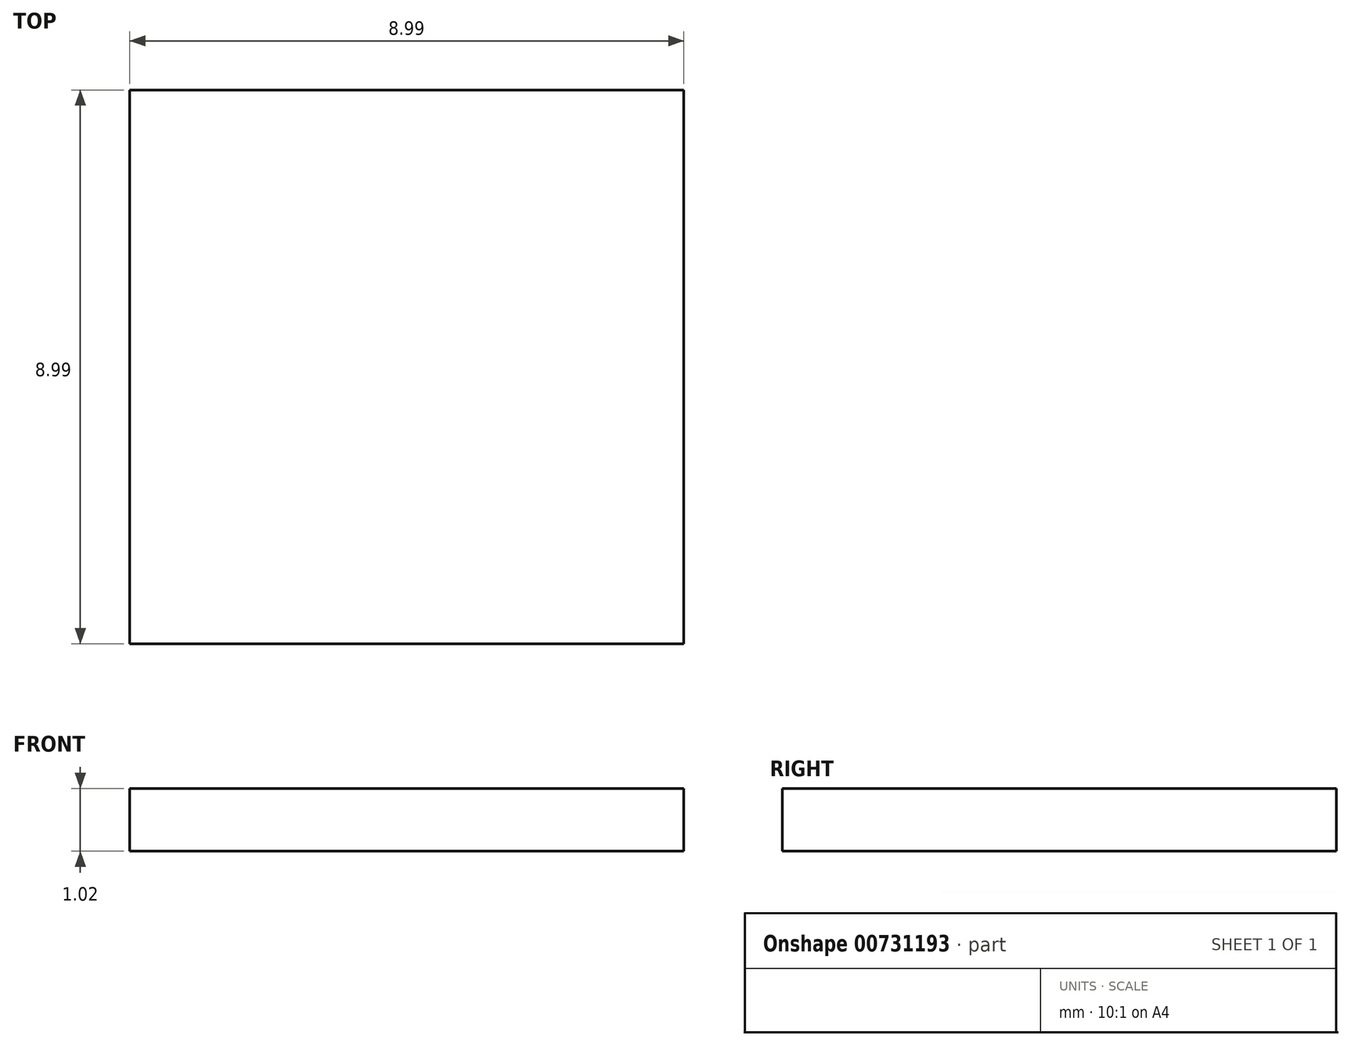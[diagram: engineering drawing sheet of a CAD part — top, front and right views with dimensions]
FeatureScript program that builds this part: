
annotation { "Feature Type Name" : "Feature", "Feature Type Description" : "" }
export const myFeature = defineFeature(function(context is Context, id is Id, definition is map)
    precondition{}
    {
        {
            var Q0;
            Q0=qCreatedBy(makeId("Top.planeOp"),FACE);
            var sketch = newSketch(context, id + "F0", { "sketchPlane" : qUnion([Q0])});
            skLineSegment(sketch, "E0", {"start": v(0, 0) * mm, "end": v(9, 0) * mm});
            skLineSegment(sketch, "E1", {"start": v(9, 0) * mm, "end": v(9, 9) * mm});
            skLineSegment(sketch, "E2", {"start": v(9, 9) * mm, "end": v(0, 9) * mm});
            skLineSegment(sketch, "E3", {"start": v(0, 9) * mm, "end": v(0, 0) * mm});
            skSolve(sketch);
        }
        {
            var Q0;
            Q0 = qSketchRegion(id + "F0", true);
            extrude(context, id + "F1", {"entities" : qUnion([Q0]), "oppositeDirection" : true, "depth" : 1.02 * mm, "offsetDistance" : 25.4 * mm});
        }
    });
